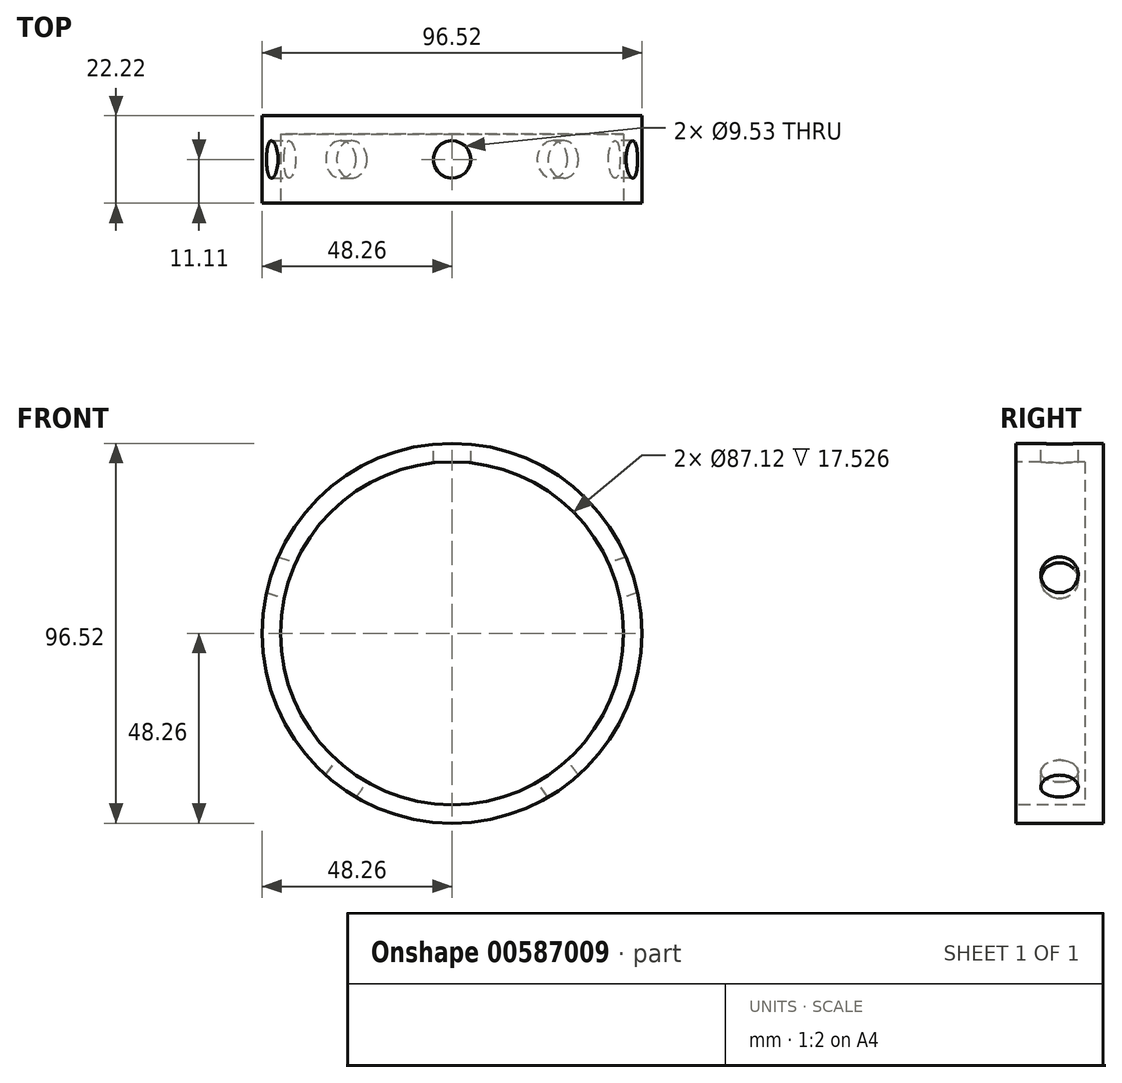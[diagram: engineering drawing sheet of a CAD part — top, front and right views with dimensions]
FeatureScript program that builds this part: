
annotation { "Feature Type Name" : "Feature", "Feature Type Description" : "" }
export const myFeature = defineFeature(function(context is Context, id is Id, definition is map)
    precondition{}
    {
        {
            var Q0;
            Q0=qCreatedBy(makeId("Right.planeOp"),FACE);
            var sketch = newSketch(context, id + "F0", { "sketchPlane" : qUnion([Q0])});
            skLineSegment(sketch, "E0.bottom", {"start": v(-11.11, 48.26) * mm, "end": v(11.11, 48.26) * mm});
            skLineSegment(sketch, "E0.top", {"start": v(-11.11, 0) * mm, "end": v(11.11, 0) * mm});
            skLineSegment(sketch, "E0.left", {"start": v(-11.11, 48.26) * mm, "end": v(-11.11, 0) * mm});
            skLineSegment(sketch, "E0.right", {"start": v(11.11, 48.26) * mm, "end": v(11.11, 0) * mm});
            skSolve(sketch);
        }
        {
            var Q0;
            Q0=makeQuery(id+"F0.imprint","IMPRINT",FACE,{"disambiguationData":[TD([[makeQuery(id+"F0.imprint","IMPRINT",EDGE,{"derivedFrom":sQuery(id+"F0.wireOp",EDGE,"E0.bottom")}),-1.0]])]});
            var Q1;
            Q1=sQuery(id+"F0.wireOp",EDGE,"E0.top");
            revolve(context, id + "F1", {"entities" : qUnion([Q0]), "axis" : qUnion([Q1]), "revolveType" : RevolveType.FULL});
        }
        {
            var Q0;
            Q0=makeQuery(id+"F1.opRevolve","SWEPT_FACE",FACE,{"disambiguationData":[OSD([sQuery(id+"F0.wireOp",EDGE,"E0.left")])]});
            shell(context, id + "F2", {"entities" : qUnion([Q0]), "thickness" : 4.7 * mm});
        }
        {
            var Q0;
            Q0=qCreatedBy(makeId("Front.planeOp"),FACE);
            var sketch = newSketch(context, id + "F3", { "sketchPlane" : qUnion([Q0])});
            skLineSegment(sketch, "E1.bottom", {"start": v(0, 61.55) * mm, "end": v(4.76, 61.55) * mm});
            skLineSegment(sketch, "E1.top", {"start": v(0, 20.16) * mm, "end": v(4.76, 20.16) * mm});
            skLineSegment(sketch, "E1.left", {"start": v(0, 61.55) * mm, "end": v(0, 20.16) * mm});
            skLineSegment(sketch, "E1.right", {"start": v(4.76, 61.55) * mm, "end": v(4.76, 20.16) * mm});
            skLineSegment(sketch, "E2.1.0", {"start": v(-57.06, 23.55) * mm, "end": v(-17.7, 10.76) * mm});
            skLineSegment(sketch, "E2.1.1", {"start": v(-58.54, 19.02) * mm, "end": v(-19.17, 6.23) * mm});
            skLineSegment(sketch, "E2.1.2", {"start": v(-19.17, 6.23) * mm, "end": v(-17.7, 10.76) * mm});
            skLineSegment(sketch, "E2.1.3", {"start": v(-58.54, 19.02) * mm, "end": v(-57.06, 23.55) * mm});
            skLineSegment(sketch, "E2.2.0", {"start": v(-40.03, -47) * mm, "end": v(-15.7, -13.5) * mm});
            skLineSegment(sketch, "E2.2.1", {"start": v(-36.18, -49.8) * mm, "end": v(-11.85, -16.3) * mm});
            skLineSegment(sketch, "E2.2.2", {"start": v(-11.85, -16.3) * mm, "end": v(-15.7, -13.5) * mm});
            skLineSegment(sketch, "E2.2.3", {"start": v(-36.18, -49.8) * mm, "end": v(-40.03, -47) * mm});
            skLineSegment(sketch, "E2.3.0", {"start": v(32.32, -52.6) * mm, "end": v(8, -19.1) * mm});
            skLineSegment(sketch, "E2.3.1", {"start": v(36.18, -49.8) * mm, "end": v(11.85, -16.3) * mm});
            skLineSegment(sketch, "E2.3.2", {"start": v(11.85, -16.3) * mm, "end": v(8, -19.1) * mm});
            skLineSegment(sketch, "E2.3.3", {"start": v(36.18, -49.8) * mm, "end": v(32.32, -52.6) * mm});
            skLineSegment(sketch, "E2.4.0", {"start": v(60, 14.5) * mm, "end": v(20.64, 1.7) * mm});
            skLineSegment(sketch, "E2.4.1", {"start": v(58.54, 19.02) * mm, "end": v(19.17, 6.23) * mm});
            skLineSegment(sketch, "E2.4.2", {"start": v(19.17, 6.23) * mm, "end": v(20.64, 1.7) * mm});
            skLineSegment(sketch, "E2.4.3", {"start": v(58.54, 19.02) * mm, "end": v(60, 14.5) * mm});
            skPoint(sketch, "E2.center", {"position": v(0, 0) * mm});
            skSolve(sketch);
        }
        {
            var Q0;
            Q0=makeQuery(id+"F3.imprint","IMPRINT",FACE,{"disambiguationData":[TD([[makeQuery(id+"F3.imprint","IMPRINT",EDGE,{"derivedFrom":sQuery(id+"F3.wireOp",EDGE,"E1.bottom")}),-1.0]])]});
            var Q1;
            Q1=sQuery(id+"F3.wireOp",EDGE,"E1.left");
            revolve(context, id + "F4", {"operationType" : NewBodyOperationType.REMOVE, "entities" : qUnion([Q0]), "axis" : qUnion([Q1]), "revolveType" : RevolveType.FULL});
        }
        {
            var Q0;
            Q0=makeQuery(id+"F3.imprint","IMPRINT",FACE,{"disambiguationData":[TD([[makeQuery(id+"F3.imprint","IMPRINT",EDGE,{"derivedFrom":sQuery(id+"F3.wireOp",EDGE,"E2.4.0")}),-1.0]])]});
            var Q1;
            Q1=sQuery(id+"F3.wireOp",EDGE,"E2.4.1");
            revolve(context, id + "F5", {"operationType" : NewBodyOperationType.REMOVE, "entities" : qUnion([Q0]), "axis" : qUnion([Q1]), "revolveType" : RevolveType.FULL, "oppositeDirection" : true});
        }
        {
            var Q0;
            Q0=makeQuery(id+"F3.imprint","IMPRINT",FACE,{"disambiguationData":[TD([[makeQuery(id+"F3.imprint","IMPRINT",EDGE,{"derivedFrom":sQuery(id+"F3.wireOp",EDGE,"E2.1.0")}),-1.0]])]});
            var Q1;
            Q1=sQuery(id+"F3.wireOp",EDGE,"E2.1.1");
            revolve(context, id + "F6", {"operationType" : NewBodyOperationType.REMOVE, "entities" : qUnion([Q0]), "axis" : qUnion([Q1]), "revolveType" : RevolveType.FULL, "oppositeDirection" : true});
        }
        {
            var Q0;
            Q0=makeQuery(id+"F3.imprint","IMPRINT",FACE,{"disambiguationData":[TD([[makeQuery(id+"F3.imprint","IMPRINT",EDGE,{"derivedFrom":sQuery(id+"F3.wireOp",EDGE,"E2.2.0")}),-1.0]])]});
            var Q1;
            Q1=sQuery(id+"F3.wireOp",EDGE,"E2.2.1");
            revolve(context, id + "F7", {"operationType" : NewBodyOperationType.REMOVE, "entities" : qUnion([Q0]), "axis" : qUnion([Q1]), "revolveType" : RevolveType.FULL, "oppositeDirection" : true});
        }
        {
            var Q0;
            Q0=makeQuery(id+"F3.imprint","IMPRINT",FACE,{"disambiguationData":[TD([[makeQuery(id+"F3.imprint","IMPRINT",EDGE,{"derivedFrom":sQuery(id+"F3.wireOp",EDGE,"E2.3.0")}),-1.0]])]});
            var Q1;
            Q1=sQuery(id+"F3.wireOp",EDGE,"E2.3.1");
            revolve(context, id + "F8", {"operationType" : NewBodyOperationType.REMOVE, "entities" : qUnion([Q0]), "axis" : qUnion([Q1]), "revolveType" : RevolveType.FULL, "oppositeDirection" : true});
        }
    });
